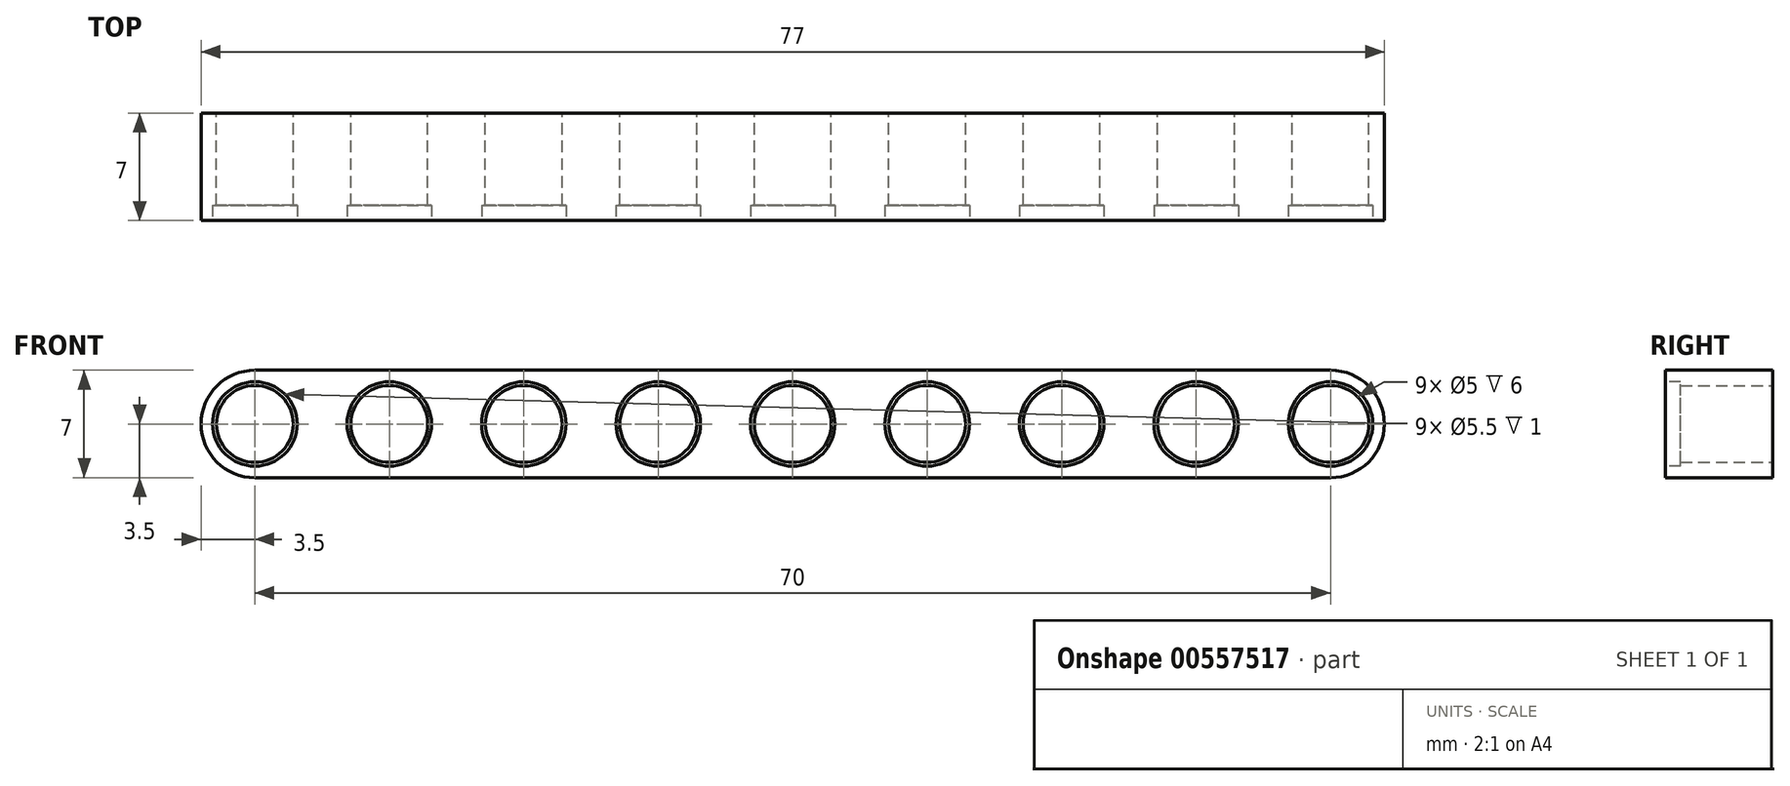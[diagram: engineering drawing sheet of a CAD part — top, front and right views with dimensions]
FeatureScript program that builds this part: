
annotation { "Feature Type Name" : "Feature", "Feature Type Description" : "" }
export const myFeature = defineFeature(function(context is Context, id is Id, definition is map)
    precondition{}
    {
        {
            var Q0;
            Q0=qCreatedBy(makeId("Front.planeOp"),FACE);
            var sketch = newSketch(context, id + "F0", { "sketchPlane" : qUnion([Q0])});
            skLineSegment(sketch, "E0.bottom", {"start": v(35, 3.5) * mm, "end": v(-35, 3.5) * mm});
            skLineSegment(sketch, "E0.top", {"start": v(35, -3.5) * mm, "end": v(-35, -3.5) * mm});
            skPoint(sketch, "E0.middle", {"position": v(0, 0) * mm});
            skArc(sketch, "E1", {"start": v(-35, 3.5) * mm, "mid": v(-38.5, 0) * mm, "end": v(-35, -3.5) * mm});
            skArc(sketch, "E2", {"start": v(35, -3.5) * mm, "mid": v(38.5, 0) * mm, "end": v(35, 3.5) * mm});
            skCircle(sketch, "E3", {"center": v(-35, 0) * mm, "radius": 2.5 * mm});
            skCircle(sketch, "E4.1.0.0", {"center": v(-26.25, 0) * mm, "radius": 2.5 * mm});
            skCircle(sketch, "E4.2.0.0", {"center": v(-17.5, 0) * mm, "radius": 2.5 * mm});
            skCircle(sketch, "E4.3.0.0", {"center": v(-8.75, 0) * mm, "radius": 2.5 * mm});
            skCircle(sketch, "E4.4.0.0", {"center": v(0, 0) * mm, "radius": 2.5 * mm});
            skCircle(sketch, "E4.5.0.0", {"center": v(8.75, 0) * mm, "radius": 2.5 * mm});
            skCircle(sketch, "E4.6.0.0", {"center": v(17.5, 0) * mm, "radius": 2.5 * mm});
            skCircle(sketch, "E4.7.0.0", {"center": v(26.25, 0) * mm, "radius": 2.5 * mm});
            skCircle(sketch, "E4.8.0.0", {"center": v(35, 0) * mm, "radius": 2.5 * mm});
            skLineSegment(sketch, "E4.direction1", {"start": v(-35, 0) * mm, "end": v(-26.25, 0) * mm, "construction": true});
            skSolve(sketch);
        }
        {
            var Q0;
            Q0 = qSketchRegion(id + "F0", true);
            extrude(context, id + "F1", {"entities" : qUnion([Q0]), "depth" : 7 * mm, "offsetDistance" : 25 * mm});
        }
        {
            var Q0;
            Q0=makeQuery(id+"F1.opExtrude","CAP_FACE",FACE,{"disambiguationData":[OSD([sQuery(id+"F0.wireOp",EDGE,"E0.bottom"),sQuery(id+"F0.wireOp",EDGE,"E0.top"),sQuery(id+"F0.wireOp",EDGE,"E1"),sQuery(id+"F0.wireOp",EDGE,"E2"),sQuery(id+"F0.wireOp",EDGE,"E3"),sQuery(id+"F0.wireOp",EDGE,"E4.1.0.0"),sQuery(id+"F0.wireOp",EDGE,"E4.2.0.0"),sQuery(id+"F0.wireOp",EDGE,"E4.3.0.0"),sQuery(id+"F0.wireOp",EDGE,"E4.4.0.0"),sQuery(id+"F0.wireOp",EDGE,"E4.5.0.0"),sQuery(id+"F0.wireOp",EDGE,"E4.6.0.0"),sQuery(id+"F0.wireOp",EDGE,"E4.7.0.0"),sQuery(id+"F0.wireOp",EDGE,"E4.8.0.0")])],"isStart":false});
            var sketch = newSketch(context, id + "F2", { "sketchPlane" : qUnion([Q0])});
            skCircle(sketch, "E5", {"center": v(35, 0) * mm, "radius": 2.75 * mm});
            skCircle(sketch, "E6.1.0.0", {"center": v(26.25, 0) * mm, "radius": 2.75 * mm});
            skCircle(sketch, "E6.2.0.0", {"center": v(17.5, 0) * mm, "radius": 2.75 * mm});
            skCircle(sketch, "E6.3.0.0", {"center": v(8.75, 0) * mm, "radius": 2.75 * mm});
            skCircle(sketch, "E6.4.0.0", {"center": v(0, 0) * mm, "radius": 2.75 * mm});
            skCircle(sketch, "E6.5.0.0", {"center": v(-8.75, 0) * mm, "radius": 2.75 * mm});
            skCircle(sketch, "E6.6.0.0", {"center": v(-17.5, 0) * mm, "radius": 2.75 * mm});
            skCircle(sketch, "E6.7.0.0", {"center": v(-26.25, 0) * mm, "radius": 2.75 * mm});
            skCircle(sketch, "E6.8.0.0", {"center": v(-35, 0) * mm, "radius": 2.75 * mm});
            skLineSegment(sketch, "E6.direction1", {"start": v(35, 0) * mm, "end": v(26.25, 0) * mm, "construction": true});
            skSolve(sketch);
        }
        {
            var Q0;
            Q0 = qSketchRegion(id + "F2", true);
            extrude(context, id + "F3", {"entities" : qUnion([Q0]), "operationType" : NewBodyOperationType.REMOVE, "oppositeDirection" : true, "depth" : 1 * mm, "offsetDistance" : 25 * mm});
        }
    });
